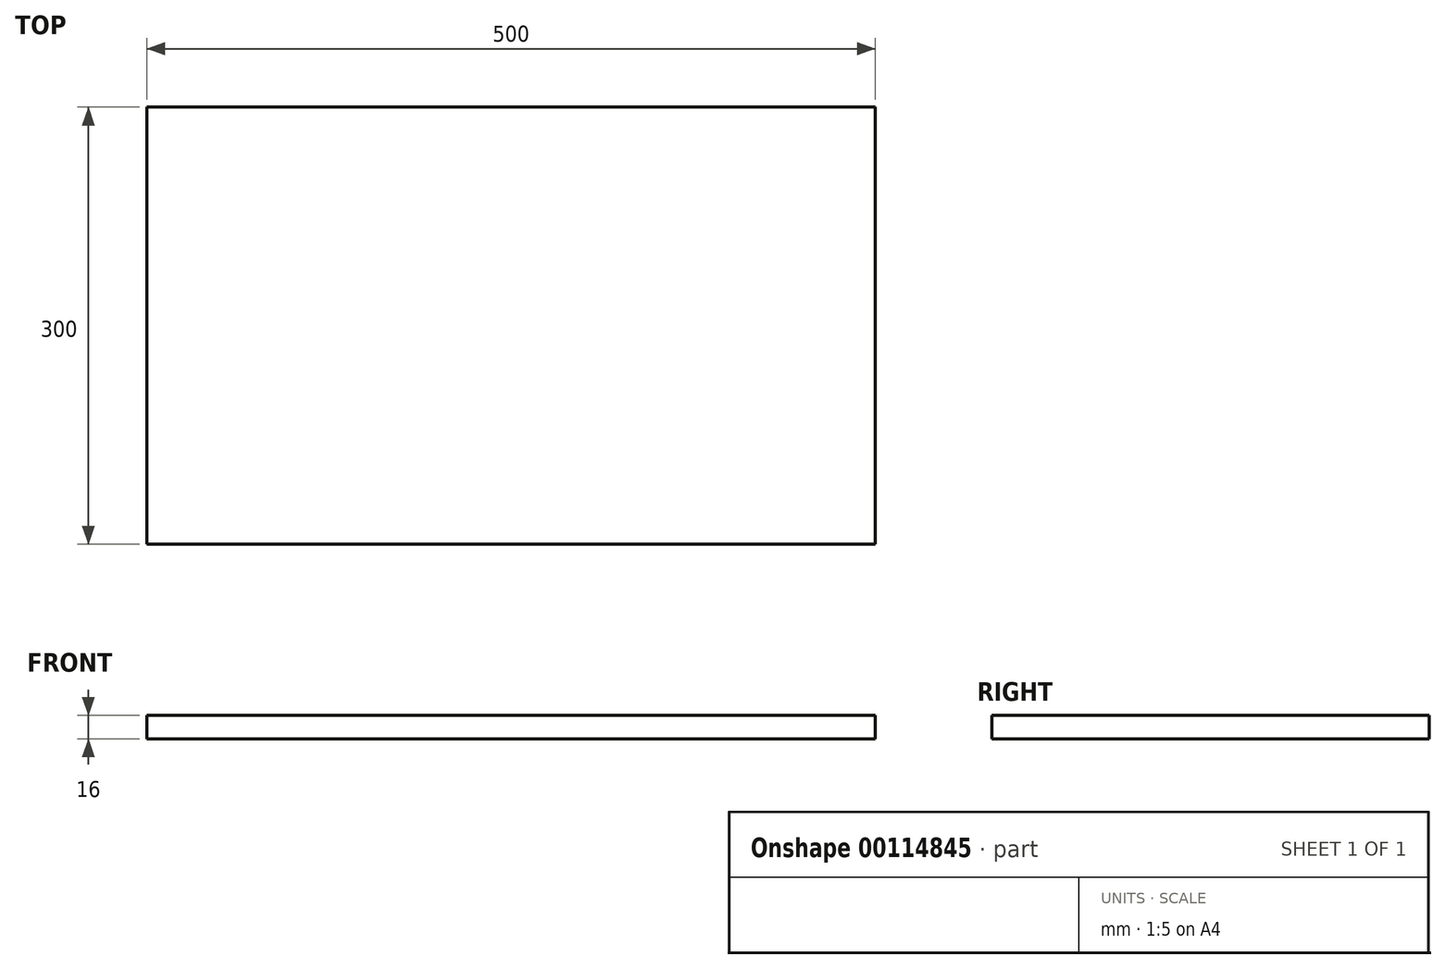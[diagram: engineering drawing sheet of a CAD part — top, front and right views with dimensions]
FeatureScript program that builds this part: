
annotation { "Feature Type Name" : "Feature", "Feature Type Description" : "" }
export const myFeature = defineFeature(function(context is Context, id is Id, definition is map)
    precondition{}
    {
        {
            var Q0;
            Q0=qCreatedBy(makeId("Top.planeOp"),FACE);
            var sketch = newSketch(context, id + "F0", { "sketchPlane" : qUnion([Q0])});
            skLineSegment(sketch, "E0.bottom", {"start": v(-250, 150) * mm, "end": v(250, 150) * mm});
            skLineSegment(sketch, "E0.top", {"start": v(-250, -150) * mm, "end": v(250, -150) * mm});
            skLineSegment(sketch, "E0.left", {"start": v(-250, 150) * mm, "end": v(-250, -150) * mm});
            skLineSegment(sketch, "E0.right", {"start": v(250, 150) * mm, "end": v(250, -150) * mm});
            skPoint(sketch, "E0.middle", {"position": v(0, 0) * mm});
            skSolve(sketch);
        }
        {
            var Q0;
            Q0=makeQuery(id+"F0.imprint","IMPRINT",FACE,{"disambiguationData":[TD([[makeQuery(id+"F0.imprint","IMPRINT",EDGE,{"derivedFrom":sQuery(id+"F0.wireOp",EDGE,"E0.bottom")}),-1.0]])]});
            extrude(context, id + "F1", {"entities" : qUnion([Q0]), "endBound" : BoundingType.SYMMETRIC, "depth" : 16 * mm});
        }
    });
